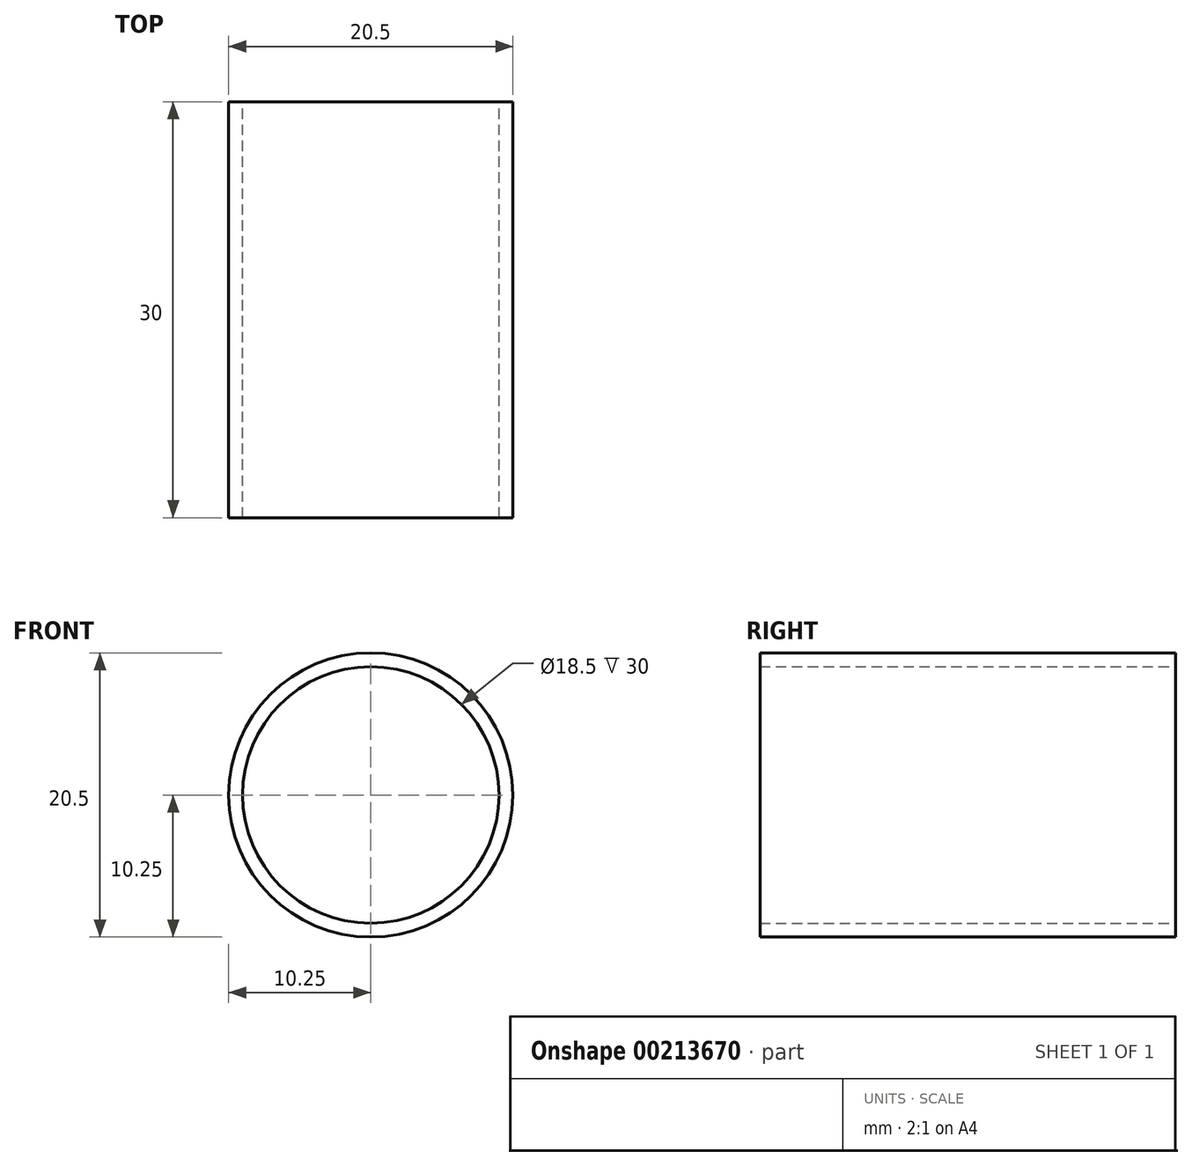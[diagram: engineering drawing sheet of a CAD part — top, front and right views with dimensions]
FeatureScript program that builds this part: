
annotation { "Feature Type Name" : "Feature", "Feature Type Description" : "" }
export const myFeature = defineFeature(function(context is Context, id is Id, definition is map)
    precondition{}
    {
        {
            var Q0;
            Q0=qCreatedBy(makeId("Front.planeOp"),FACE);
            var sketch = newSketch(context, id + "F0", { "sketchPlane" : qUnion([Q0])});
            skCircle(sketch, "E0", {"center": v(0, 0) * mm, "radius": 9.25 * mm});
            skCircle(sketch, "E1", {"center": v(0, 0) * mm, "radius": 10.25 * mm});
            skSolve(sketch);
        }
        {
            var Q0;
            Q0 = qSketchRegion(id + "F0", true);
            extrude(context, id + "F1", {"entities" : qUnion([Q0]), "depth" : 30 * mm});
        }
    });
